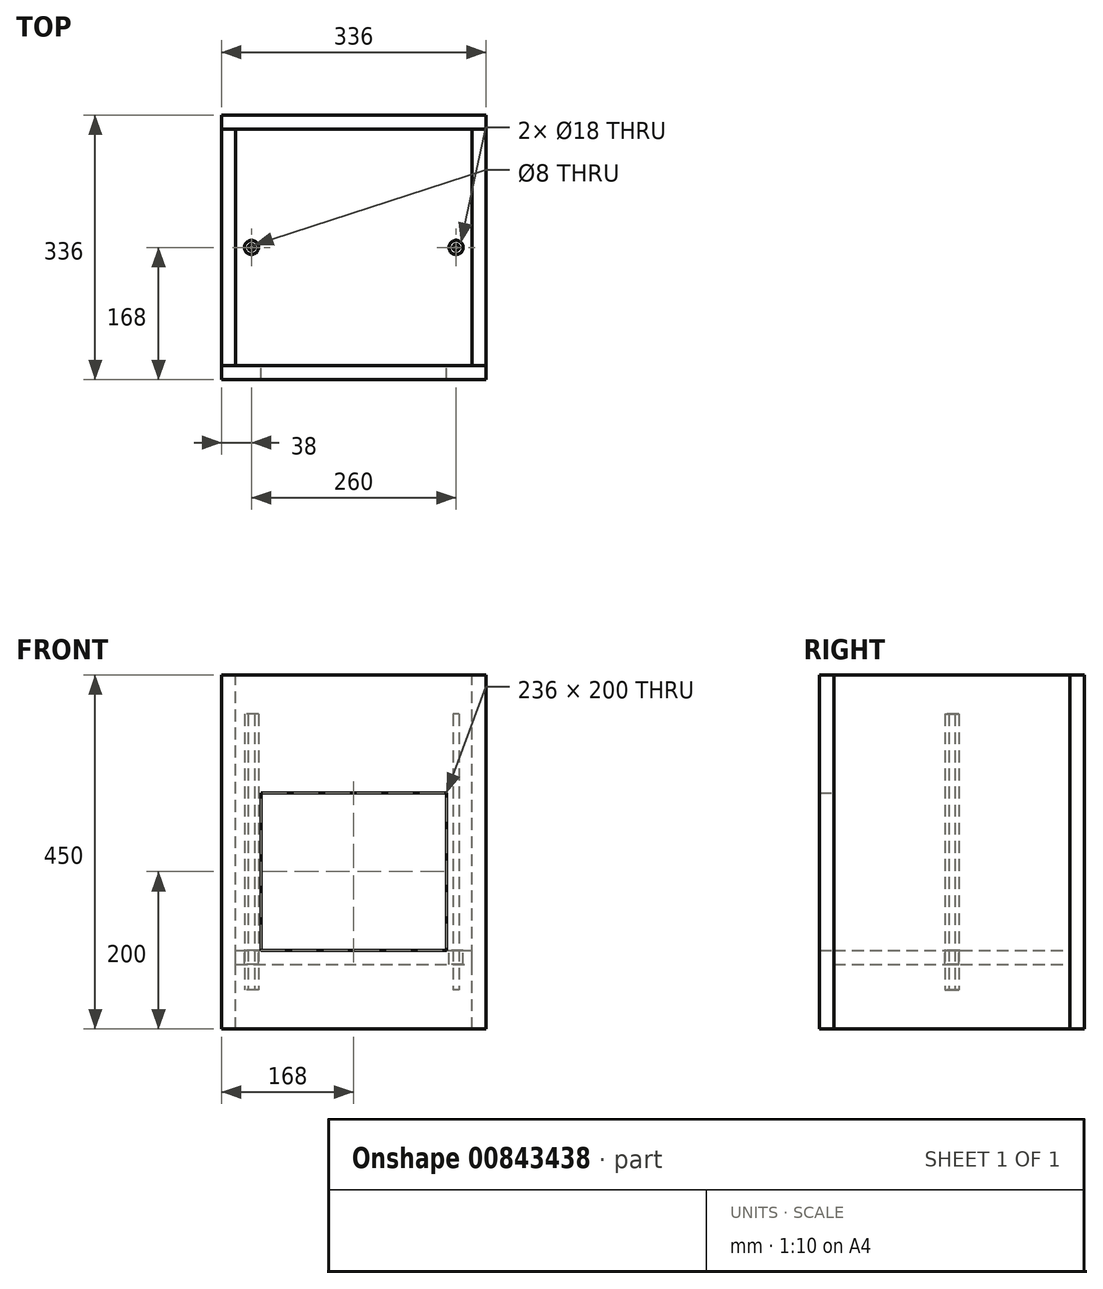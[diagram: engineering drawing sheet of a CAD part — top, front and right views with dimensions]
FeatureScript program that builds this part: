
annotation { "Feature Type Name" : "Feature", "Feature Type Description" : "" }
export const myFeature = defineFeature(function(context is Context, id is Id, definition is map)
    precondition{}
    {
        {
            var Q0;
            Q0=qCreatedBy(makeId("Top.planeOp"),FACE);
            var sketch = newSketch(context, id + "F0", { "sketchPlane" : qUnion([Q0])});
            skLineSegment(sketch, "E0.bottom", {"start": v(150, 150) * mm, "end": v(-150, 150) * mm});
            skLineSegment(sketch, "E0.top", {"start": v(150, -150) * mm, "end": v(-150, -150) * mm});
            skLineSegment(sketch, "E0.left", {"start": v(150, 150) * mm, "end": v(150, -150) * mm});
            skLineSegment(sketch, "E0.right", {"start": v(-150, 150) * mm, "end": v(-150, -150) * mm});
            skPoint(sketch, "E0.middle", {"position": v(0, 0) * mm});
            skSolve(sketch);
        }
        {
            var Q0;
            Q0=makeQuery(id+"F0.imprint","IMPRINT",FACE,{"disambiguationData":[TD([[makeQuery(id+"F0.imprint","IMPRINT",EDGE,{"derivedFrom":sQuery(id+"F0.wireOp",EDGE,"E0.bottom")}),1.0]])]});
            var Q1;
            Q1=sQuery(id+"F0.wireOp",EDGE,"E0.right");
            var Q2;
            Q2=sQuery(id+"F0.wireOp",EDGE,"E0.bottom");
            var Q3;
            Q3=sQuery(id+"F0.wireOp",EDGE,"E0.top");
            var Q4;
            Q4=sQuery(id+"F0.wireOp",EDGE,"E0.left");
            extrude(context, id + "F1", {"entities" : qUnion([Q0]), "bodyType" : ToolBodyType.SURFACE, "surfaceEntities" : qUnion([Q1, Q2, Q3, Q4]), "depth" : 450 * mm, "offsetDistance" : 25 * mm});
        }
        {
            assignVariable(context, id + "F2", {"name" : "SheetThickness", "anyValue" : 18});
        }
        {
            var Q0;
            Q0=makeQuery(id+"F1.opExtrude","SWEPT_FACE",FACE,{"disambiguationData":[OSD([sQuery(id+"F0.wireOp",EDGE,"E0.left")])]});
            extrude(context, id + "F3", {"entities" : qUnion([Q0]), "depth" : (getVariable(context, 'SheetThickness')) * mm, "offsetDistance" : 25 * mm});
        }
        {
            var Q0;
            Q0=makeQuery(id+"F3.opExtrude","SWEPT_BODY",BODY,{"disambiguationData":[OSD([sQuery(id+"F0.wireOp",EDGE,"E0.left")])]});
            var Q1;
            Q1=qCreatedBy(makeId("Right.planeOp"),FACE);
            mirror(context, id + "F4", {"entities" : qUnion([Q0]), "mirrorPlane" : qUnion([Q1])});
        }
        {
            var Q0;
            Q0=makeQuery(id+"F1.opExtrude","SWEPT_FACE",FACE,{"disambiguationData":[OSD([sQuery(id+"F0.wireOp",EDGE,"E0.bottom")])]});
            var sketch = newSketch(context, id + "F5", { "sketchPlane" : qUnion([Q0])});
            skLineSegment(sketch, "E1.bottom", {"start": v(-168, 450) * mm, "end": v(168, 450) * mm});
            skLineSegment(sketch, "E1.top", {"start": v(-168, 0) * mm, "end": v(168, 0) * mm});
            skLineSegment(sketch, "E1.left", {"start": v(-168, 450) * mm, "end": v(-168, 0) * mm});
            skLineSegment(sketch, "E1.right", {"start": v(168, 450) * mm, "end": v(168, 0) * mm});
            skSolve(sketch);
        }
        {
            var Q0;
            Q0 = qSketchRegion(id + "F5", true);
            extrude(context, id + "F6", {"entities" : qUnion([Q0]), "depth" : (getVariable(context, 'SheetThickness')) * mm, "offsetDistance" : 25 * mm});
        }
        {
            var Q0;
            Q0=makeQuery(id+"F1.opExtrude","SWEPT_FACE",FACE,{"disambiguationData":[OSD([sQuery(id+"F0.wireOp",EDGE,"E0.top")])]});
            var sketch = newSketch(context, id + "F7", { "sketchPlane" : qUnion([Q0])});
            skLineSegment(sketch, "E2.bottom", {"start": v(-168, 450) * mm, "end": v(168, 450) * mm});
            skLineSegment(sketch, "E2.top", {"start": v(-168, 300) * mm, "end": v(168, 300) * mm});
            skLineSegment(sketch, "E2.left", {"start": v(-168, 450) * mm, "end": v(-168, 300) * mm});
            skLineSegment(sketch, "E2.right", {"start": v(168, 450) * mm, "end": v(168, 300) * mm});
            skLineSegment(sketch, "E3.bottom", {"start": v(-168, 0) * mm, "end": v(168, 0) * mm});
            skLineSegment(sketch, "E3.top", {"start": v(-168, 100) * mm, "end": v(168, 100) * mm});
            skLineSegment(sketch, "E3.left", {"start": v(-168, 0) * mm, "end": v(-168, 100) * mm});
            skLineSegment(sketch, "E3.right", {"start": v(168, 0) * mm, "end": v(168, 100) * mm});
            skLineSegment(sketch, "E4.bottom", {"start": v(-168, 300) * mm, "end": v(-118, 300) * mm});
            skLineSegment(sketch, "E4.top", {"start": v(-168, 100) * mm, "end": v(-118, 100) * mm});
            skLineSegment(sketch, "E4.left", {"start": v(-168, 300) * mm, "end": v(-168, 100) * mm});
            skLineSegment(sketch, "E4.right", {"start": v(-118, 300) * mm, "end": v(-118, 100) * mm});
            skLineSegment(sketch, "E5.bottom", {"start": v(168, 300) * mm, "end": v(118, 300) * mm});
            skLineSegment(sketch, "E5.top", {"start": v(168, 100) * mm, "end": v(118, 100) * mm});
            skLineSegment(sketch, "E5.left", {"start": v(168, 300) * mm, "end": v(168, 100) * mm});
            skLineSegment(sketch, "E5.right", {"start": v(118, 300) * mm, "end": v(118, 100) * mm});
            skSolve(sketch);
        }
        {
            var Q0;
            Q0 = qSketchRegion(id + "F7", true);
            extrude(context, id + "F8", {"entities" : qUnion([Q0]), "depth" : (getVariable(context, 'SheetThickness')) * mm, "offsetDistance" : 25 * mm});
        }
        {
            var Q0;
            Q0=qCreatedBy(makeId("Top.planeOp"),FACE);
            cPlane(context, id + "F9", {"entities" : qUnion([Q0]), "cplaneType" : CPlaneType.OFFSET, "offset" : 100 * mm, "width" : 150 * mm, "height" : 150 * mm});
        }
        {
            var Q0;
            Q0=qCreatedBy(id+"F9.planeOp",FACE);
            var sketch = newSketch(context, id + "F10", { "sketchPlane" : qUnion([Q0])});
            skLineSegment(sketch, "E6.bottom", {"start": v(-150, -150) * mm, "end": v(150, -150) * mm});
            skLineSegment(sketch, "E6.top", {"start": v(-150, 150) * mm, "end": v(150, 150) * mm});
            skLineSegment(sketch, "E6.left", {"start": v(-150, -150) * mm, "end": v(-150, 150) * mm});
            skLineSegment(sketch, "E6.right", {"start": v(150, -150) * mm, "end": v(150, 150) * mm});
            skSolve(sketch);
        }
        {
            var Q0;
            Q0 = qSketchRegion(id + "F10", true);
            extrude(context, id + "F11", {"entities" : qUnion([Q0]), "oppositeDirection" : true, "depth" : (getVariable(context, 'SheetThickness')) * mm, "offsetDistance" : 25 * mm});
        }
        {
            var Q0;
            Q0=qCreatedBy(id+"F9.planeOp",FACE);
            var sketch = newSketch(context, id + "F12", { "sketchPlane" : qUnion([Q0])});
            skCircle(sketch, "E7", {"center": v(130, 0) * mm, "radius": 4 * mm});
            skLineSegment(sketch, "E8", {"start": v(0, 150) * mm, "end": v(0, -150) * mm, "construction": true});
            skLineSegment(sketch, "E9", {"start": v(0, 0) * mm, "end": v(130, 0) * mm, "construction": true});
            skCircle(sketch, "E10", {"center": v(130, 0) * mm, "radius": 9 * mm});
            skCircle(sketch, "E11.MirrorC", {"center": v(-130, 0) * mm, "radius": 4 * mm});
            skCircle(sketch, "E12.MirrorC", {"center": v(-130, 0) * mm, "radius": 9 * mm});
            skSolve(sketch);
        }
        {
            var Q0;
            Q0=makeQuery(id+"F12.imprint","IMPRINT",FACE,{"disambiguationData":[TD([[makeQuery(id+"F12.imprint","IMPRINT",EDGE,{"derivedFrom":sQuery(id+"F12.wireOp",EDGE,"E7")}),-1.0]])]});
            var Q1;
            Q1=makeQuery(id+"F12.imprint","IMPRINT",FACE,{"disambiguationData":[TD([[makeQuery(id+"F12.imprint","IMPRINT",EDGE,{"derivedFrom":sQuery(id+"F12.wireOp",EDGE,"E7")}),1.0]])]});
            var Q2;
            Q2=makeQuery(id+"F12.imprint","IMPRINT",FACE,{"disambiguationData":[TD([[makeQuery(id+"F12.imprint","IMPRINT",EDGE,{"derivedFrom":sQuery(id+"F12.wireOp",EDGE,"E11.MirrorC")}),1.0]])]});
            var Q3;
            Q3=makeQuery(id+"F12.imprint","IMPRINT",FACE,{"disambiguationData":[TD([[makeQuery(id+"F12.imprint","IMPRINT",EDGE,{"derivedFrom":sQuery(id+"F12.wireOp",EDGE,"E11.MirrorC")}),-1.0]])]});
            extrude(context, id + "F13", {"entities" : qUnion([Q0, Q1, Q2, Q3]), "operationType" : NewBodyOperationType.REMOVE, "endBound" : BoundingType.THROUGH_ALL, "oppositeDirection" : true, "depth" : 25 * mm, "offsetDistance" : 25 * mm});
        }
        {
            var Q0;
            Q0=makeQuery(id+"F12.imprint","IMPRINT",FACE,{"disambiguationData":[TD([[makeQuery(id+"F12.imprint","IMPRINT",EDGE,{"derivedFrom":sQuery(id+"F12.wireOp",EDGE,"E7")}),1.0]])]});
            var Q1;
            Q1=makeQuery(id+"F12.imprint","IMPRINT",FACE,{"disambiguationData":[TD([[makeQuery(id+"F12.imprint","IMPRINT",EDGE,{"derivedFrom":sQuery(id+"F12.wireOp",EDGE,"E11.MirrorC")}),-1.0]])]});
            extrude(context, id + "F14", {"entities" : qUnion([Q0, Q1]), "depth" : 300 * mm, "offsetDistance" : 25 * mm, "hasSecondDirection" : true, "secondDirectionOppositeDirection" : true, "secondDirectionDepth" : 50 * mm});
        }
    });
